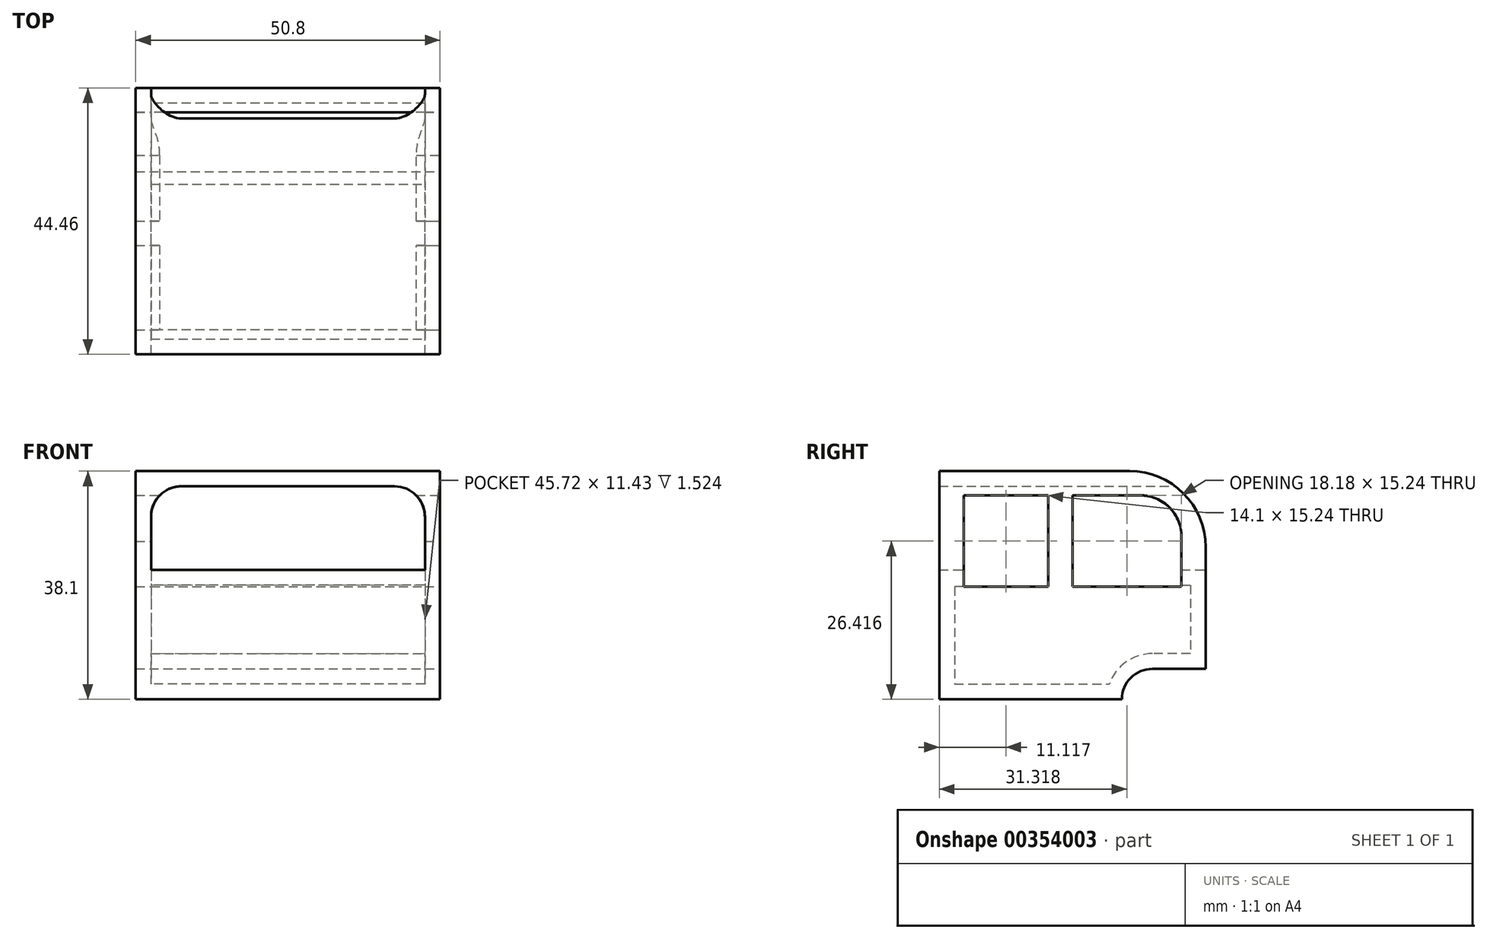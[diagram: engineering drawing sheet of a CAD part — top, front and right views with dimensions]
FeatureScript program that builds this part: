
annotation { "Feature Type Name" : "Feature", "Feature Type Description" : "" }
export const myFeature = defineFeature(function(context is Context, id is Id, definition is map)
    precondition{}
    {
        {
            var Q0;
            Q0=qCreatedBy(makeId("Top.planeOp"),FACE);
            var sketch = newSketch(context, id + "F0", { "sketchPlane" : qUnion([Q0])});
            skLineSegment(sketch, "E0.bottom", {"start": v(25.4, -22.22) * mm, "end": v(-25.4, -22.23) * mm});
            skLineSegment(sketch, "E0.top", {"start": v(25.4, 22.23) * mm, "end": v(-25.4, 22.22) * mm});
            skLineSegment(sketch, "E0.left", {"start": v(25.4, -22.23) * mm, "end": v(25.4, 22.23) * mm});
            skLineSegment(sketch, "E0.right", {"start": v(-25.4, -22.23) * mm, "end": v(-25.4, 22.22) * mm});
            skPoint(sketch, "E0.middle", {"position": v(0, 0) * mm});
            skSolve(sketch);
        }
        {
            var Q0;
            Q0 = qSketchRegion(id + "F0", true);
            extrude(context, id + "F1", {"entities" : qUnion([Q0]), "depth" : 38.1 * mm});
        }
        {
            var Q0;
            Q0=makeQuery(id+"F1.opExtrude","SWEPT_FACE",FACE,{"disambiguationData":[OSD([sQuery(id+"F0.wireOp",EDGE,"E0.left")])]});
            var sketch = newSketch(context, id + "F2", { "sketchPlane" : qUnion([Q0])});
            skLineSegment(sketch, "E1.bottom", {"start": v(22.23, 0) * mm, "end": v(8.26, 0) * mm});
            skLineSegment(sketch, "E1.top", {"start": v(22.23, 5.08) * mm, "end": v(8.26, 5.08) * mm});
            skLineSegment(sketch, "E1.left", {"start": v(22.23, 0) * mm, "end": v(22.23, 5.08) * mm});
            skLineSegment(sketch, "E1.right", {"start": v(8.26, 0) * mm, "end": v(8.26, 5.08) * mm});
            skSolve(sketch);
        }
        {
            var Q0;
            Q0 = qSketchRegion(id + "F2", true);
            extrude(context, id + "F3", {"entities" : qUnion([Q0]), "operationType" : NewBodyOperationType.REMOVE, "oppositeDirection" : true, "depth" : 50.8 * mm});
        }
        {
            var Q0;
            Q0=makeQuery(id+"F1.opExtrude","CAP_EDGE",EDGE,{"disambiguationData":[OSD([sQuery(id+"F0.wireOp",EDGE,"E0.top")])],"isStart":false});
            fillet(context, id + "F4", {"entities" : qUnion([Q0]), "radius" : 12.7 * mm, "tangentPropagation" : true, "allowEdgeOverflow" : false});
        }
        {
            var Q0;
            Q0=makeQuery(id+"F1.opExtrude","SWEPT_FACE",FACE,{"disambiguationData":[OSD([sQuery(id+"F0.wireOp",EDGE,"E0.top")])]});
            var sketch = newSketch(context, id + "F5", { "sketchPlane" : qUnion([Q0])});
            skLineSegment(sketch, "E2.bottom", {"start": v(-22.86, 21.59) * mm, "end": v(22.86, 21.59) * mm});
            skLineSegment(sketch, "E2.top", {"start": v(-22.86, 35.56) * mm, "end": v(22.86, 35.56) * mm});
            skLineSegment(sketch, "E2.left", {"start": v(-22.86, 35.56) * mm, "end": v(-22.86, 21.59) * mm});
            skLineSegment(sketch, "E2.right", {"start": v(22.86, 35.56) * mm, "end": v(22.86, 21.59) * mm});
            skSolve(sketch);
        }
        {
            var Q0;
            Q0 = qSketchRegion(id + "F5", true);
            extrude(context, id + "F6", {"entities" : qUnion([Q0]), "operationType" : NewBodyOperationType.REMOVE, "oppositeDirection" : true, "depth" : 50.8 * mm});
        }
        {
            var Q0;
            Q0=makeQuery(id+"F6.boolean.opBoolean","COPY",EDGE,{"derivedFrom":makeQuery(id+"F6.opExtrude","SWEPT_EDGE",EDGE,{"disambiguationData":[OSD([sQuery(id+"F5.wireOp",EDGE,"E2.top"),sQuery(id+"F5.wireOp",EDGE,"E2.left")])]})});
            var Q1;
            Q1=makeQuery(id+"F6.boolean.opBoolean","COPY",EDGE,{"derivedFrom":makeQuery(id+"F6.opExtrude","SWEPT_EDGE",EDGE,{"disambiguationData":[OSD([sQuery(id+"F5.wireOp",EDGE,"E2.top"),sQuery(id+"F5.wireOp",EDGE,"E2.right")])]})});
            fillet(context, id + "F7", {"entities" : qUnion([Q0, Q1]), "radius" : 5.08 * mm, "tangentPropagation" : true, "allowEdgeOverflow" : false});
        }
        {
            var Q0;
            Q0=makeQuery(id+"F1.opExtrude","SWEPT_FACE",FACE,{"disambiguationData":[OSD([sQuery(id+"F0.wireOp",EDGE,"E0.left")])]});
            var sketch = newSketch(context, id + "F8", { "sketchPlane" : qUnion([Q0])});
            skCircle(sketch, "E3", {"center": v(11.33, 27.16) * mm, "radius": 6.88 * mm});
            skLineSegment(sketch, "E4", {"start": v(18.16, 27.98) * mm, "end": v(18.16, 18.8) * mm});
            skLineSegment(sketch, "E5", {"start": v(18.16, 18.8) * mm, "end": v(0, 18.8) * mm});
            skLineSegment(sketch, "E6", {"start": v(10.98, 34.04) * mm, "end": v(0, 34.04) * mm});
            skLineSegment(sketch, "E7", {"start": v(0, 34.04) * mm, "end": v(0, 18.8) * mm});
            skLineSegment(sketch, "E8", {"start": v(-4.06, 34.04) * mm, "end": v(-4.06, 18.8) * mm});
            skLineSegment(sketch, "E9", {"start": v(-4.06, 34.04) * mm, "end": v(-18.16, 34.04) * mm});
            skPoint(sketch, "E10.start.orphan", {"position": v(-18.16, 18.8) * mm});
            skLineSegment(sketch, "E11", {"start": v(-18.16, 34.04) * mm, "end": v(-18.16, 18.8) * mm});
            skLineSegment(sketch, "E12", {"start": v(-4.06, 18.8) * mm, "end": v(-18.16, 18.8) * mm});
            skSolve(sketch);
        }
        {
            var Q0;
            Q0 = qSketchRegion(id + "F8", true);
            extrude(context, id + "F9", {"entities" : qUnion([Q0]), "operationType" : NewBodyOperationType.REMOVE, "oppositeDirection" : true, "depth" : 50.8 * mm});
        }
        {
            var Q0;
            Q0=makeQuery(id+"F3.boolean.opBoolean","COPY",EDGE,{"derivedFrom":makeQuery(id+"F3.opExtrude","SWEPT_EDGE",EDGE,{"disambiguationData":[OSD([sQuery(id+"F2.wireOp",EDGE,"E1.top"),sQuery(id+"F2.wireOp",EDGE,"E1.right")])]})});
            fillet(context, id + "F10", {"entities" : qUnion([Q0]), "radius" : 5.08 * mm, "tangentPropagation" : true, "allowEdgeOverflow" : false});
        }
        {
            var Q0;
            Q0=makeQuery(id+"F9.boolean.opBoolean","COPY",FACE,{"derivedFrom":makeQuery(id+"F9.opExtrude","SWEPT_FACE",FACE,{"disambiguationData":[OSD([sQuery(id+"F8.wireOp",EDGE,"E8")])]})});
            var Q1;
            Q1=makeQuery(id+"F9.boolean.opBoolean","COPY",FACE,{"derivedFrom":makeQuery(id+"F9.opExtrude","SWEPT_FACE",FACE,{"disambiguationData":[OSD([sQuery(id+"F8.wireOp",EDGE,"E7")])]})});
            var Q2;
            Q2=makeQuery(id+"F9.boolean.opBoolean","COPY",FACE,{"derivedFrom":makeQuery(id+"F9.opExtrude","SWEPT_FACE",FACE,{"disambiguationData":[OSD([sQuery(id+"F8.wireOp",EDGE,"E5")])]})});
            var Q3;
            Q3=makeQuery(id+"F9.boolean.opBoolean","COPY",FACE,{"derivedFrom":makeQuery(id+"F9.opExtrude","SWEPT_FACE",FACE,{"disambiguationData":[OSD([sQuery(id+"F8.wireOp",EDGE,"E12")])]})});
            var Q4;
            Q4=makeQuery(id+"F9.boolean.opBoolean","SPLIT",FACE,{"disambiguationData":[TD([makeQuery(id+"F9.opExtrude","SWEPT_FACE",FACE,{"disambiguationData":[OSD([sQuery(id+"F8.wireOp",EDGE,"E7")])]})])],"derivedFrom":makeQuery(id+"F6.boolean.opBoolean","COPY",FACE,{"derivedFrom":makeQuery(id+"F6.opExtrude","SWEPT_FACE",FACE,{"disambiguationData":[OSD([sQuery(id+"F5.wireOp",EDGE,"E2.bottom")])]})})});
            var Q5;
            Q5=makeQuery(id+"F9.boolean.opBoolean","COPY",FACE,{"derivedFrom":makeQuery(id+"F9.opExtrude","SWEPT_FACE",FACE,{"disambiguationData":[OSD([sQuery(id+"F8.wireOp",EDGE,"E4")])]})});
            shell(context, id + "F11", {"entities" : qUnion([Q0, Q1, Q2, Q3, Q4, Q5]), "thickness" : 2.54 * mm});
        }
    });
